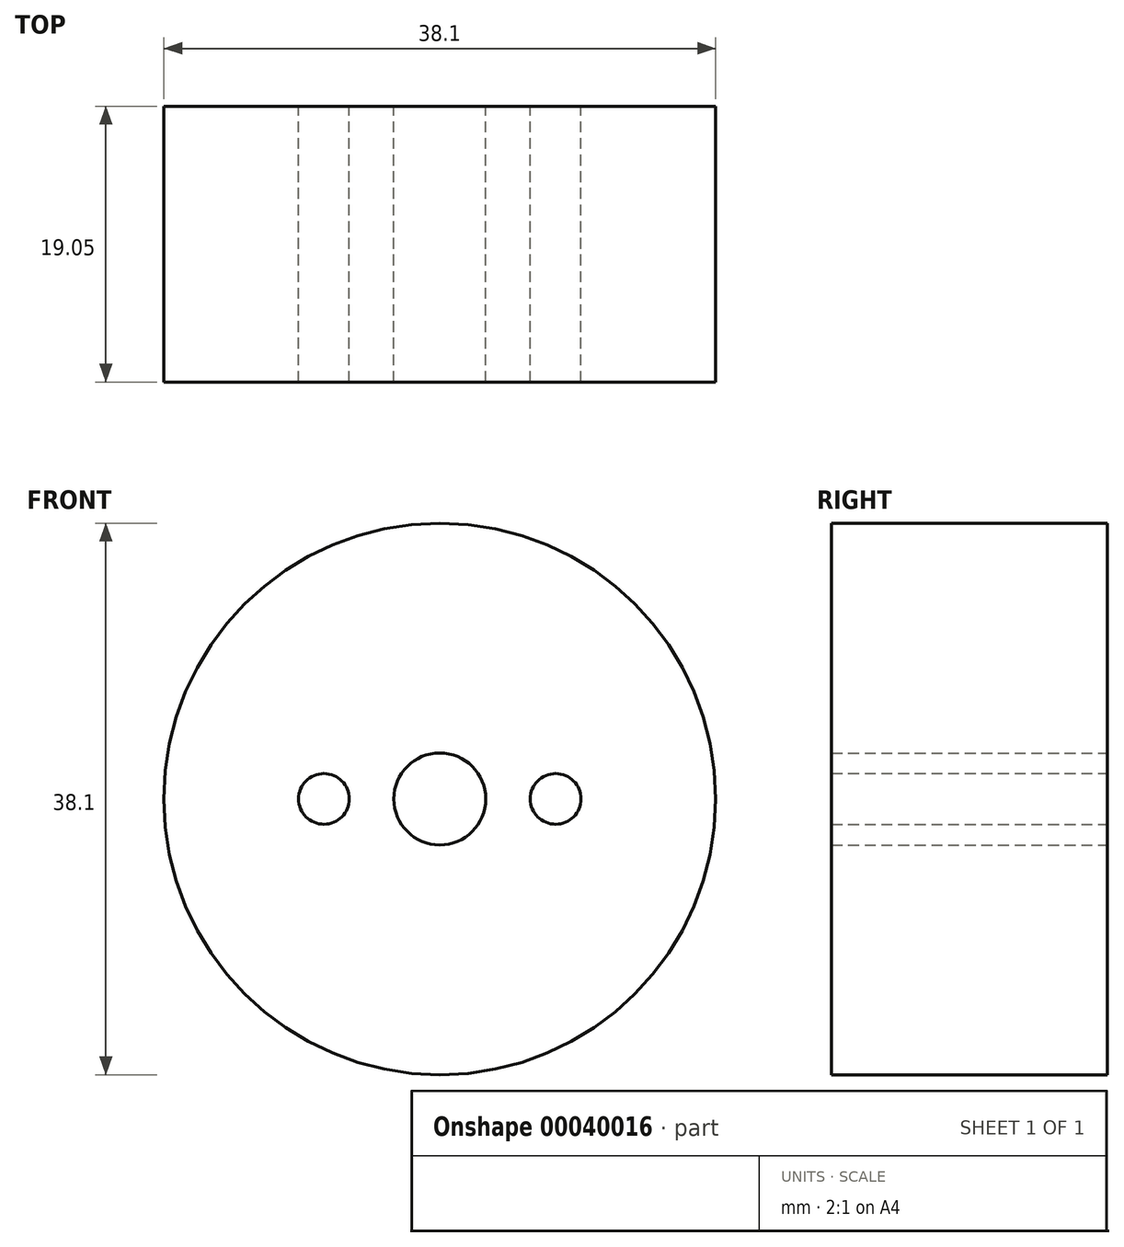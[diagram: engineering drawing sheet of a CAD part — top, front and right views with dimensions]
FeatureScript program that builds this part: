
annotation { "Feature Type Name" : "Feature", "Feature Type Description" : "" }
export const myFeature = defineFeature(function(context is Context, id is Id, definition is map)
    precondition{}
    {
        {
            var Q0;
            Q0=qCreatedBy(makeId("Front.planeOp"),FACE);
            var sketch = newSketch(context, id + "F0", { "sketchPlane" : qUnion([Q0])});
            skCircle(sketch, "E0", {"center": v(0, 0) * mm, "radius": 19.05 * mm});
            skCircle(sketch, "E1", {"center": v(0, 0) * mm, "radius": 3.18 * mm});
            skCircle(sketch, "E2", {"center": v(8, 0) * mm, "radius": 1.75 * mm});
            skCircle(sketch, "E3", {"center": v(-8, 0) * mm, "radius": 1.75 * mm});
            skSolve(sketch);
        }
        {
            var Q0;
            Q0=makeQuery(id+"F0.imprint","IMPRINT",FACE,{"disambiguationData":[TD([[makeQuery(id+"F0.imprint","IMPRINT",EDGE,{"derivedFrom":sQuery(id+"F0.wireOp",EDGE,"E0")}),1.0]])]});
            extrude(context, id + "F1", {"entities" : qUnion([Q0]), "depth" : 19.05 * mm});
        }
    });
